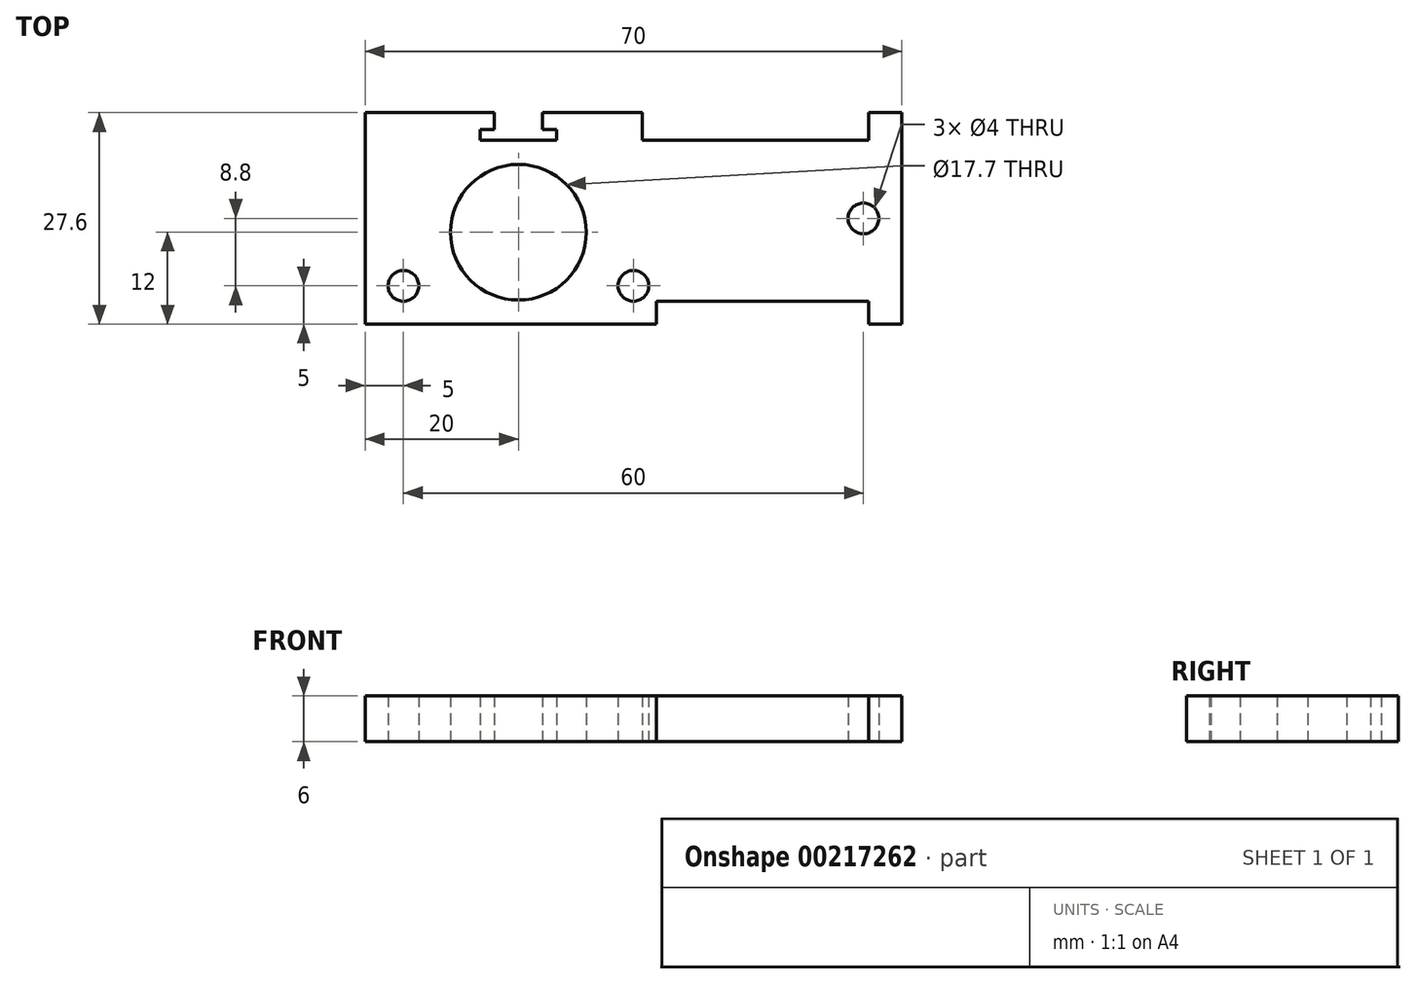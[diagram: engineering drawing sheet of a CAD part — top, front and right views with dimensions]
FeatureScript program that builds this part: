
annotation { "Feature Type Name" : "Feature", "Feature Type Description" : "" }
export const myFeature = defineFeature(function(context is Context, id is Id, definition is map)
    precondition{}
    {
        {
            var Q0;
            Q0=qCreatedBy(makeId("Top.planeOp"),FACE);
            var sketch = newSketch(context, id + "F0", { "sketchPlane" : qUnion([Q0])});
            skLineSegment(sketch, "E0.right", {"start": v(-20, 12) * mm, "end": v(-20, -12) * mm});
            skPoint(sketch, "E0.middle", {"position": v(0, 0) * mm});
            skCircle(sketch, "E1", {"center": v(0, 0) * mm, "radius": 8.85 * mm});
            skLineSegment(sketch, "E2", {"start": v(-20, 12) * mm, "end": v(-20, 15.6) * mm});
            skLineSegment(sketch, "E3", {"start": v(-20, 15.6) * mm, "end": v(-3.15, 15.6) * mm});
            skLineSegment(sketch, "E4", {"start": v(-3.15, 15.6) * mm, "end": v(-3.15, 13.4) * mm});
            skLineSegment(sketch, "E5", {"start": v(-3.15, 13.4) * mm, "end": v(-5, 13.4) * mm});
            skLineSegment(sketch, "E6", {"start": v(-5, 13.4) * mm, "end": v(-5, 12) * mm});
            skLineSegment(sketch, "E7", {"start": v(3.15, 15.6) * mm, "end": v(3.15, 13.4) * mm});
            skLineSegment(sketch, "E8", {"start": v(3.15, 13.4) * mm, "end": v(5, 13.4) * mm});
            skLineSegment(sketch, "E9", {"start": v(5, 13.4) * mm, "end": v(5, 12) * mm});
            skCircle(sketch, "E10", {"center": v(-15, -7) * mm, "radius": 2 * mm});
            skCircle(sketch, "E11", {"center": v(15, -7) * mm, "radius": 2 * mm});
            skLineSegment(sketch, "E12", {"start": v(50, 15.6) * mm, "end": v(50, -12) * mm});
            skCircle(sketch, "E13", {"center": v(45, 1.8) * mm, "radius": 2 * mm});
            skLineSegment(sketch, "E14", {"start": v(16.15, 15.6) * mm, "end": v(16.15, 12) * mm});
            skLineSegment(sketch, "E15", {"start": v(5, 12) * mm, "end": v(-5, 12) * mm});
            skLineSegment(sketch, "E16", {"start": v(16.15, 12) * mm, "end": v(45.65, 12) * mm});
            skLineSegment(sketch, "E17", {"start": v(45.65, 12) * mm, "end": v(45.65, 15.6) * mm});
            skLineSegment(sketch, "E18", {"start": v(3.15, 15.6) * mm, "end": v(16.15, 15.6) * mm});
            skLineSegment(sketch, "E19", {"start": v(45.65, 15.6) * mm, "end": v(50, 15.6) * mm});
            skLineSegment(sketch, "E20", {"start": v(18, -9) * mm, "end": v(45.65, -9) * mm});
            skLineSegment(sketch, "E21", {"start": v(18, -9) * mm, "end": v(18, -12) * mm});
            skLineSegment(sketch, "E22", {"start": v(45.65, -9) * mm, "end": v(45.65, -12) * mm});
            skLineSegment(sketch, "E23", {"start": v(50, -12) * mm, "end": v(45.65, -12) * mm});
            skLineSegment(sketch, "E24", {"start": v(18, -12) * mm, "end": v(-20, -12) * mm});
            skSolve(sketch);
        }
        {
            var Q0;
            Q0=makeQuery(id+"F0.imprint","IMPRINT",FACE,{"disambiguationData":[TD([[makeQuery(id+"F0.imprint","IMPRINT",EDGE,{"derivedFrom":sQuery(id+"F0.wireOp",EDGE,"E0.top")}),-1.0]])]});
            var Q1;
            {var subQ0=sQuery(id+"F0.wireOp",EDGE,"Dwna2OCW-YsBe-wcoT-JuqE-rApbmNP8ZqE2");Q1=makeQuery(id+"F0.imprint","IMPRINT",FACE,{"disambiguationData":[TD([[makeQuery(id+"F0.imprint","IMPRINT",EDGE,{"derivedFrom":subQ0}),1.0]])]});}
            var Q2;
            {var subQ0=sQuery(id+"F0.wireOp",EDGE,"E2");Q2=makeQuery(id+"F0.imprint","IMPRINT",FACE,{"disambiguationData":[TD([[makeQuery(id+"F0.imprint","IMPRINT",EDGE,{"derivedFrom":subQ0}),-1.0]])]});}
            var Q3;
            Q3=makeQuery(id+"F0.imprint","IMPRINT",FACE,{"disambiguationData":[TD([[makeQuery(id+"F0.imprint","IMPRINT",EDGE,{"derivedFrom":sQuery(id+"F0.wireOp",EDGE,"E0.left")}),1.0]])]});
            extrude(context, id + "F1", {"entities" : qUnion([Q0, Q1, Q2, Q3]), "depth" : 6 * mm});
        }
    });
